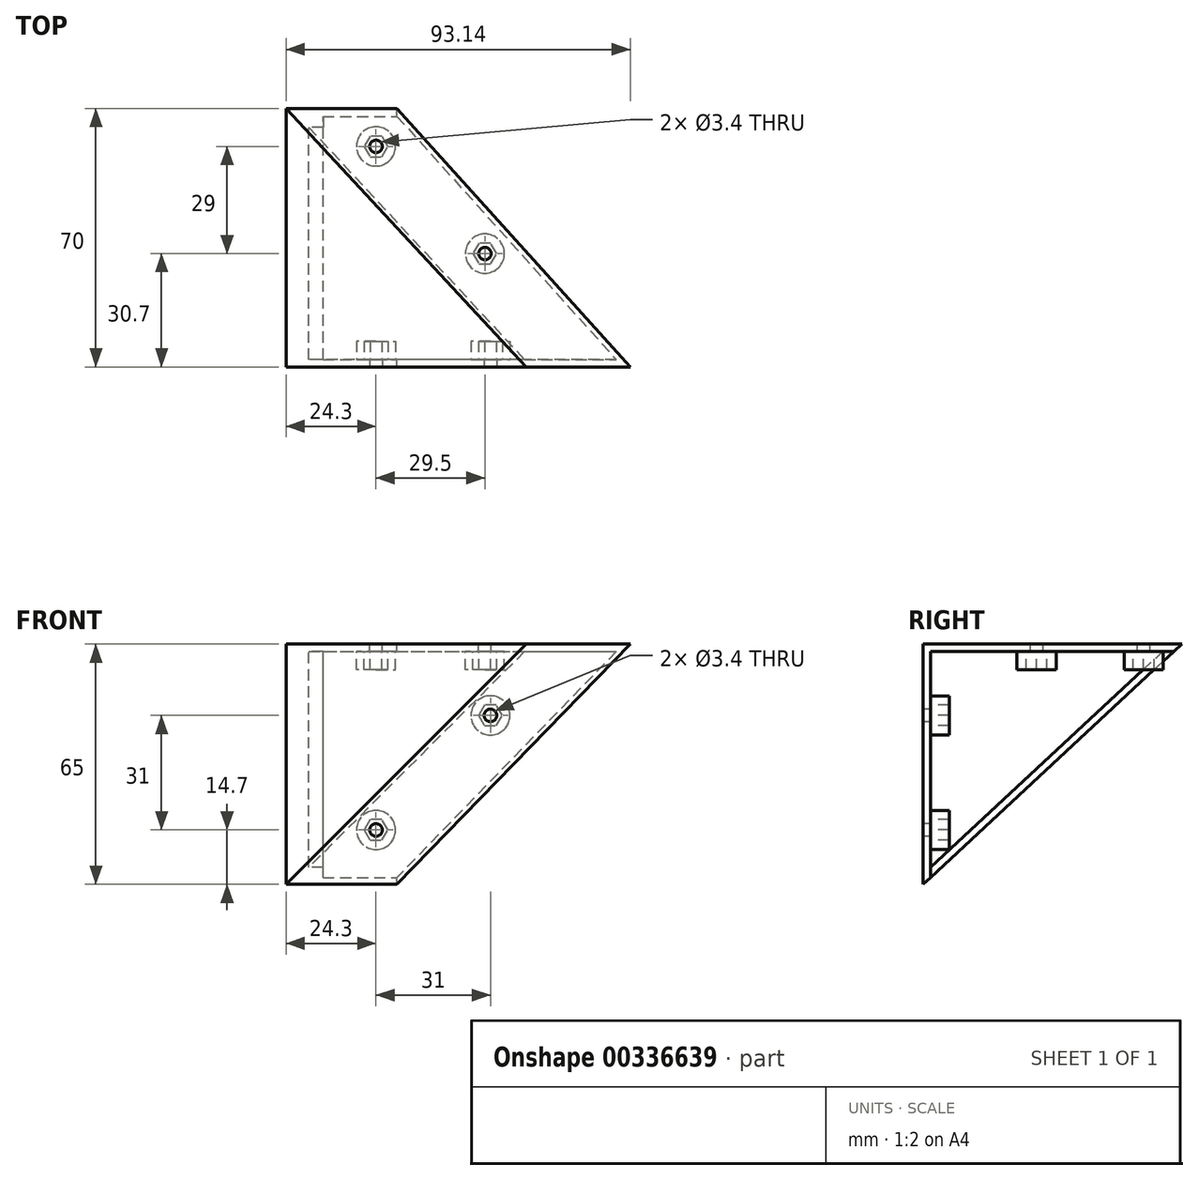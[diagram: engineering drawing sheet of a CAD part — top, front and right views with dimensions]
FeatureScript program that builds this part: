
annotation { "Feature Type Name" : "Feature", "Feature Type Description" : "" }
export const myFeature = defineFeature(function(context is Context, id is Id, definition is map)
    precondition{}
    {
        {
            var Q0;
            Q0=qCreatedBy(makeId("Front.planeOp"),FACE);
            var sketch = newSketch(context, id + "F0", { "sketchPlane" : qUnion([Q0])});
            skLineSegment(sketch, "E0", {"start": v(-300, 0) * mm, "end": v(0, 0) * mm});
            skLineSegment(sketch, "E1", {"start": v(0, 0) * mm, "end": v(0, 175) * mm});
            skLineSegment(sketch, "E2", {"start": v(0, 175) * mm, "end": v(-30, 175) * mm});
            skLineSegment(sketch, "E3", {"start": v(-30, 175) * mm, "end": v(-30, 95) * mm});
            skLineSegment(sketch, "E4", {"start": v(-30, 95) * mm, "end": v(-70, 95) * mm});
            skLineSegment(sketch, "E5", {"start": v(-70, 95) * mm, "end": v(-75, 90) * mm});
            skLineSegment(sketch, "E6", {"start": v(-75, 90) * mm, "end": v(-75, 85) * mm});
            skLineSegment(sketch, "E7", {"start": v(-75, 85) * mm, "end": v(-140, 20) * mm});
            skLineSegment(sketch, "E8", {"start": v(-140, 20) * mm, "end": v(-300, 20) * mm});
            skLineSegment(sketch, "E9", {"start": v(-300, 20) * mm, "end": v(-300, 0) * mm});
            skSolve(sketch);
        }
        {
            var Q0;
            Q0 = qSketchRegion(id + "F0", true);
            extrude(context, id + "F1", {"entities" : qUnion([Q0]), "depth" : 5 * mm, "offsetDistance" : 25 * mm});
        }
        {
            var Q0;
            Q0=makeQuery(id+"F1.opExtrude","SWEPT_FACE",FACE,{"disambiguationData":[OSD([sQuery(id+"F0.wireOp",EDGE,"E0")])]});
            cPlane(context, id + "F2", {"entities" : qUnion([Q0]), "cplaneType" : CPlaneType.OFFSET, "offset" : 85 * mm, "oppositeDirection" : true, "width" : 150 * mm, "height" : 150 * mm});
        }
        {
            var Q0;
            Q0=qCreatedBy(id+"F2.planeOp",FACE);
            var sketch = newSketch(context, id + "F3", { "sketchPlane" : qUnion([Q0])});
            skLineSegment(sketch, "E10", {"start": v(0, 0) * mm, "end": v(-70, 0) * mm});
            skLineSegment(sketch, "E11", {"start": v(-70, 0) * mm, "end": v(-140, -70) * mm});
            skLineSegment(sketch, "E12", {"start": v(-140, -70) * mm, "end": v(-300, -70) * mm});
            skLineSegment(sketch, "E13", {"start": v(-300, -70) * mm, "end": v(-300, -157.82) * mm});
            skLineSegment(sketch, "E14", {"start": v(-300, -157.82) * mm, "end": v(0, -157.82) * mm});
            skLineSegment(sketch, "E15", {"start": v(0, -157.82) * mm, "end": v(0, 0) * mm});
            skSolve(sketch);
        }
        {
            var Q0;
            Q0=makeQuery(id+"F3.imprint","IMPRINT",FACE,{"disambiguationData":[TD([[makeQuery(id+"F3.imprint","IMPRINT",EDGE,{"derivedFrom":sQuery(id+"F3.wireOp",EDGE,"E10")}),1.0]])]});
            extrude(context, id + "F4", {"entities" : qUnion([Q0]), "operationType" : NewBodyOperationType.ADD, "oppositeDirection" : true, "depth" : 5 * mm, "offsetDistance" : 25 * mm});
        }
        {
            var Q0;
            Q0=makeQuery(id+"F4.opExtrude","CAP_VERTEX",VERTEX,{"disambiguationData":[OSD([sQuery(id+"F3.wireOp",EDGE,"E12"),sQuery(id+"F3.wireOp",EDGE,"E13")])],"isStart":true});
            var Q1;
            Q1=sQuery(id+"F0.wireOp",VERTEX,"E9.start");
            var Q2;
            Q2=sQuery(id+"F0.wireOp",VERTEX,"E8.start");
            cPlane(context, id + "F5", {"entities" : qUnion([Q0, Q1, Q2]), "cplaneType" : CPlaneType.THREE_POINT, "offset" : 25 * mm, "width" : 150 * mm, "height" : 150 * mm});
        }
        {
            var Q0;
            Q0=qCreatedBy(id+"F5.planeOp",FACE);
            var sketch = newSketch(context, id + "F6", { "sketchPlane" : qUnion([Q0])});
            skLineSegment(sketch, "E16", {"start": v(-140, -109.13) * mm, "end": v(-140, -13.6) * mm});
            skLineSegment(sketch, "E17", {"start": v(-140, -13.6) * mm, "end": v(-300, -13.6) * mm});
            skLineSegment(sketch, "E18", {"start": v(-300, -13.6) * mm, "end": v(-300, -109.13) * mm});
            skLineSegment(sketch, "E19", {"start": v(-300, -109.13) * mm, "end": v(-140, -109.13) * mm});
            skSolve(sketch);
        }
        {
            var Q0;
            Q0=qSketchRegion(id+"F0",true);
            extrude(context, id + "F7", {"entities" : qUnion([Q0]), "depth" : 5.42 * mm});
        }
        {
            var Q0;
            Q0=qCreatedBy(id+"F5.planeOp",FACE);
            var sketch = newSketch(context, id + "F8", { "sketchPlane" : qUnion([Q0])});
            skLineSegment(sketch, "E20", {"start": v(-140, -109.13) * mm, "end": v(-140, -13.6) * mm});
            skLineSegment(sketch, "E21", {"start": v(-140, -13.6) * mm, "end": v(-110, -13.6) * mm});
            skLineSegment(sketch, "E22", {"start": v(-110, -13.6) * mm, "end": v(-110, -109.13) * mm});
            skLineSegment(sketch, "E23", {"start": v(-110, -109.13) * mm, "end": v(-140, -109.13) * mm});
            skSolve(sketch);
        }
        {
            var Q0;
            Q0=sQuery(id+"F0.wireOp",VERTEX,"E7.start");
            var Q1;
            Q1=sQuery(id+"F8.wireOp",VERTEX,"E20.start");
            var Q2;
            Q2=sQuery(id+"F8.wireOp",VERTEX,"E21.start");
            cPlane(context, id + "F9", {"entities" : qUnion([Q0, Q1, Q2]), "cplaneType" : CPlaneType.THREE_POINT, "offset" : 25 * mm, "width" : 150 * mm, "height" : 150 * mm});
        }
        {
            var Q0;
            Q0=qCreatedBy(id+"F9.planeOp",FACE);
            var sketch = newSketch(context, id + "F10", { "sketchPlane" : qUnion([Q0])});
            skLineSegment(sketch, "E24", {"start": v(145.84, -38.9) * mm, "end": v(62.1, -84.85) * mm});
            skLineSegment(sketch, "E25", {"start": v(62.1, -84.85) * mm, "end": v(62.1, 7.07) * mm});
            skLineSegment(sketch, "E26", {"start": v(62.1, 7.07) * mm, "end": v(145.84, -38.9) * mm});
            skSolve(sketch);
        }
        {
            var Q0;
            Q0 = qSketchRegion(id + "F10", true);
            extrude(context, id + "F11", {"entities" : qUnion([Q0]), "operationType" : NewBodyOperationType.ADD, "depth" : 2 * mm, "offsetDistance" : 25 * mm});
        }
        {
            var Q0;
            Q0=makeQuery(id+"F4.opExtrude","CAP_VERTEX",VERTEX,{"disambiguationData":[OSD([sQuery(id+"F3.wireOp",EDGE,"E10"),sQuery(id+"F3.wireOp",EDGE,"E11")])],"isStart":true});
            var Q1;
            Q1=sQuery(id+"F0.wireOp",VERTEX,"E7.start");
            var Q2;
            Q2=sQuery(id+"F6.wireOp",VERTEX,"E19.end");
            cPlane(context, id + "F12", {"entities" : qUnion([Q0, Q1, Q2]), "cplaneType" : CPlaneType.THREE_POINT, "offset" : 25 * mm, "width" : 150 * mm, "height" : 150 * mm});
        }
        {
            var Q0;
            Q0=qCreatedBy(id+"F12.planeOp",FACE);
            var sketch = newSketch(context, id + "F13", { "sketchPlane" : qUnion([Q0])});
            skLineSegment(sketch, "E27", {"start": v(-70, 0) * mm, "end": v(-75, 0) * mm});
            skLineSegment(sketch, "E28", {"start": v(-75, 0) * mm, "end": v(-140, 70) * mm});
            skLineSegment(sketch, "E29", {"start": v(-140, 70) * mm, "end": v(-70, 0) * mm});
            skSolve(sketch);
        }
        {
            var Q0;
            Q0=makeQuery(id+"F13.imprint","IMPRINT",FACE,{"disambiguationData":[TD([[makeQuery(id+"F13.imprint","IMPRINT",EDGE,{"derivedFrom":sQuery(id+"F13.wireOp",EDGE,"E27")}),-1.0]])]});
            extrude(context, id + "F14", {"entities" : qUnion([Q0]), "oppositeDirection" : true, "depth" : 2 * mm, "offsetDistance" : 25 * mm});
        }
        {
            var Q0;
            Q0=makeQuery(id+"F8.imprint","IMPRINT",FACE,{"disambiguationData":[TD([[makeQuery(id+"F8.imprint","IMPRINT",EDGE,{"derivedFrom":sQuery(id+"F8.wireOp",EDGE,"E20")}),-1.0]])]});
            extrude(context, id + "F15", {"entities" : qUnion([Q0]), "oppositeDirection" : true, "depth" : 2 * mm, "offsetDistance" : 25 * mm});
        }
        {
            var Q0;
            Q0=makeQuery(id+"F0.imprint","IMPRINT",FACE,{"disambiguationData":[TD([[makeQuery(id+"F0.imprint","IMPRINT",EDGE,{"derivedFrom":sQuery(id+"F0.wireOp",EDGE,"E0")}),1.0]])]});
            var sketch = newSketch(context, id + "F16", { "sketchPlane" : qUnion([Q0])});
            skLineSegment(sketch, "E30", {"start": v(-75, 85) * mm, "end": v(-45, 85) * mm});
            skLineSegment(sketch, "E31", {"start": v(-45, 85) * mm, "end": v(-110, 20) * mm});
            skLineSegment(sketch, "E32", {"start": v(-110, 20) * mm, "end": v(-140, 20) * mm});
            skLineSegment(sketch, "E33", {"start": v(-140, 20) * mm, "end": v(-75, 85) * mm});
            skSolve(sketch);
        }
        {
            var Q0;
            Q0=makeQuery(id+"F4.opExtrude","CAP_FACE",FACE,{"disambiguationData":[OSD([sQuery(id+"F3.wireOp",EDGE,"E10"),sQuery(id+"F3.wireOp",EDGE,"E11"),sQuery(id+"F3.wireOp",EDGE,"E12"),sQuery(id+"F3.wireOp",EDGE,"E13"),sQuery(id+"F3.wireOp",EDGE,"E14"),sQuery(id+"F3.wireOp",EDGE,"E15")])],"isStart":true});
            extrude(context, id + "F17", {"entities" : qUnion([Q0]), "operationType" : NewBodyOperationType.REMOVE, "oppositeDirection" : true, "depth" : 102.5 * mm, "offsetDistance" : 25 * mm});
        }
        {
            var Q0;
            Q0=makeQuery(id+"F16.imprint","IMPRINT",FACE,{"disambiguationData":[TD([[makeQuery(id+"F16.imprint","IMPRINT",EDGE,{"derivedFrom":sQuery(id+"F16.wireOp",EDGE,"E30")}),-1.0]])]});
            extrude(context, id + "F18", {"entities" : qUnion([Q0]), "operationType" : NewBodyOperationType.ADD, "oppositeDirection" : true, "depth" : 2 * mm, "offsetDistance" : 25 * mm});
        }
        {
            var Q0;
            Q0=makeQuery(id+"F0.imprint","IMPRINT",FACE,{"disambiguationData":[TD([[makeQuery(id+"F0.imprint","IMPRINT",EDGE,{"derivedFrom":sQuery(id+"F0.wireOp",EDGE,"E0")}),1.0]])]});
            extrude(context, id + "F19", {"entities" : qUnion([Q0]), "operationType" : NewBodyOperationType.REMOVE, "depth" : 239 * mm, "offsetDistance" : 25 * mm});
        }
        {
            var Q0;
            Q0=sQuery(id+"F0.wireOp",VERTEX,"E7.start");
            var Q1;
            Q1=makeQuery(id+"F18.opExtrude","CAP_VERTEX",VERTEX,{"disambiguationData":[OSD([sQuery(id+"F16.wireOp",EDGE,"E30"),sQuery(id+"F16.wireOp",EDGE,"E31")])],"isStart":false});
            var Q2;
            Q2=makeQuery(id+"F15.opExtrude","CAP_VERTEX",VERTEX,{"disambiguationData":[OSD([sQuery(id+"F8.wireOp",EDGE,"E22"),sQuery(id+"F8.wireOp",EDGE,"E23")])],"isStart":true});
            cPlane(context, id + "F20", {"entities" : qUnion([Q0, Q1, Q2]), "cplaneType" : CPlaneType.THREE_POINT, "offset" : 25 * mm, "width" : 150 * mm, "height" : 150 * mm});
        }
        {
            var Q0;
            Q0=qCreatedBy(id+"F20.planeOp",FACE);
            var sketch = newSketch(context, id + "F21", { "sketchPlane" : qUnion([Q0])});
            skLineSegment(sketch, "E34", {"start": v(-45, 0) * mm, "end": v(-110, -70) * mm});
            skLineSegment(sketch, "E35", {"start": v(-110, -70) * mm, "end": v(-140, -70) * mm});
            skLineSegment(sketch, "E36", {"start": v(-140, -70) * mm, "end": v(-75, 0) * mm});
            skLineSegment(sketch, "E37", {"start": v(-75, 0) * mm, "end": v(-45, 0) * mm});
            skSolve(sketch);
        }
        {
            var Q0;
            Q0 = qSketchRegion(id + "F21", true);
            extrude(context, id + "F22", {"entities" : qUnion([Q0]), "operationType" : NewBodyOperationType.ADD, "depth" : 2 * mm, "offsetDistance" : 25 * mm});
        }
        {
            var Q0;
            Q0=sQuery(id+"F6.wireOp",VERTEX,"E17.start");
            var Q1;
            Q1=sQuery(id+"F6.wireOp",VERTEX,"E19.end");
            var Q2;
            {var subQ0=sQuery(id+"F8.wireOp",EDGE,"E22");Q2=makeQuery(id+"F18.boolean.opBoolean","INTERSECT",VERTEX,{"derivedFrom":[makeQuery(id+"F15.opExtrude","CAP_FACE",FACE,{"disambiguationData":[OSD([sQuery(id+"F8.wireOp",EDGE,"E20"),sQuery(id+"F8.wireOp",EDGE,"E21"),subQ0,sQuery(id+"F8.wireOp",EDGE,"E23")])],"isStart":true}),makeQuery(id+"F15.opExtrude","SWEPT_FACE",FACE,{"disambiguationData":[OSD([subQ0])]}),makeQuery(id+"F18.opExtrude","CAP_FACE",FACE,{"disambiguationData":[OSD([sQuery(id+"F16.wireOp",EDGE,"E30"),sQuery(id+"F16.wireOp",EDGE,"E31"),sQuery(id+"F16.wireOp",EDGE,"E32"),sQuery(id+"F16.wireOp",EDGE,"E33")])],"isStart":false})]});}
            cPlane(context, id + "F23", {"entities" : qUnion([Q0, Q1, Q2]), "cplaneType" : CPlaneType.THREE_POINT, "offset" : 25 * mm, "width" : 150 * mm, "height" : 150 * mm});
        }
        {
            var Q0;
            Q0=qCreatedBy(id+"F23.planeOp",FACE);
            var sketch = newSketch(context, id + "F24", { "sketchPlane" : qUnion([Q0])});
            skLineSegment(sketch, "E38", {"start": v(-152.04, 9.78) * mm, "end": v(-152.04, 115.97) * mm});
            skLineSegment(sketch, "E39", {"start": v(-152.04, 115.97) * mm, "end": v(-52.48, 115.97) * mm});
            skLineSegment(sketch, "E40", {"start": v(-52.48, 115.97) * mm, "end": v(-52.48, 8.15) * mm});
            skLineSegment(sketch, "E41", {"start": v(-52.48, 8.15) * mm, "end": v(-152.04, 9.78) * mm});
            skSolve(sketch);
        }
        {
            var Q0;
            Q0 = qSketchRegion(id + "F24", true);
            extrude(context, id + "F25", {"entities" : qUnion([Q0]), "operationType" : NewBodyOperationType.REMOVE, "oppositeDirection" : true, "depth" : 25 * mm, "offsetDistance" : 25 * mm});
        }
        {
            var Q0;
            Q0=sQuery(id+"F6.wireOp",VERTEX,"E19.end");
            var Q1;
            Q1=sQuery(id+"F6.wireOp",VERTEX,"E17.start");
            var Q2;
            Q2=sQuery(id+"F0.wireOp",VERTEX,"E7.start");
            cPlane(context, id + "F26", {"entities" : qUnion([Q0, Q1, Q2]), "cplaneType" : CPlaneType.THREE_POINT, "offset" : 25 * mm, "width" : 150 * mm, "height" : 150 * mm});
        }
        {
            var Q0;
            Q0=qCreatedBy(id+"F26.planeOp",FACE);
            var sketch = newSketch(context, id + "F27", { "sketchPlane" : qUnion([Q0])});
            skLineSegment(sketch, "E42.bottom", {"start": v(59.1, -93.53) * mm, "end": v(160.86, -93.53) * mm});
            skLineSegment(sketch, "E42.top", {"start": v(59.1, -19.2) * mm, "end": v(160.86, -19.2) * mm});
            skLineSegment(sketch, "E42.left", {"start": v(59.1, -93.53) * mm, "end": v(59.1, -19.2) * mm});
            skLineSegment(sketch, "E42.right", {"start": v(160.86, -93.53) * mm, "end": v(160.86, -19.2) * mm});
            skPoint(sketch, "E42.middle", {"position": v(109.98, -56.36) * mm});
            skSolve(sketch);
        }
        {
            var Q0;
            Q0 = qSketchRegion(id + "F27", true);
            extrude(context, id + "F28", {"entities" : qUnion([Q0]), "operationType" : NewBodyOperationType.REMOVE, "oppositeDirection" : true, "depth" : 25 * mm, "offsetDistance" : 25 * mm});
        }
        {
            var Q0;
            {var subQ0=sQuery(id+"F13.wireOp",EDGE,"E29");var subQ3=sQuery(id+"F16.wireOp",EDGE,"E30");var subQ8=sQuery(id+"F16.wireOp",EDGE,"E31");var subQ9=makeQuery(id+"F18.opExtrude","SWEPT_FACE",FACE,{"disambiguationData":[OSD([subQ8])]});var subQ10=sQuery(id+"F16.wireOp",EDGE,"E32");Q0=makeQuery(id+"F22.boolean.opBoolean","INTERSECT",VERTEX,{"derivedFrom":[subQ9,makeQuery(id+"F18.boolean.opBoolean","SPLIT",FACE,{"disambiguationData":[TD([makeQuery(id+"F14.opExtrude","SWEPT_FACE",FACE,{"disambiguationData":[OSD([subQ0])]})])],"derivedFrom":makeQuery(id+"F18.opExtrude","CAP_FACE",FACE,{"disambiguationData":[OSD([subQ3,subQ8,subQ10,sQuery(id+"F16.wireOp",EDGE,"E33")])],"isStart":false})}),makeQuery(id+"F22.opExtrude","CAP_FACE",FACE,{"disambiguationData":[OSD([sQuery(id+"F21.wireOp",EDGE,"E34"),sQuery(id+"F21.wireOp",EDGE,"E35"),sQuery(id+"F21.wireOp",EDGE,"E36"),sQuery(id+"F21.wireOp",EDGE,"E37")])],"isStart":false})]});}
            var Q1;
            Q1=makeQuery(id+"F22.boolean.opBoolean","INTERSECT",VERTEX,{"derivedFrom":[makeQuery(id+"F18.opExtrude","SWEPT_FACE",FACE,{"disambiguationData":[OSD([sQuery(id+"F16.wireOp",EDGE,"E31")])]}),makeQuery(id+"F22.opExtrude","CAP_FACE",FACE,{"disambiguationData":[OSD([sQuery(id+"F21.wireOp",EDGE,"E34"),sQuery(id+"F21.wireOp",EDGE,"E35"),sQuery(id+"F21.wireOp",EDGE,"E36"),sQuery(id+"F21.wireOp",EDGE,"E37")])],"isStart":false})]});
            var Q2;
            {var subQ0=sQuery(id+"F13.wireOp",EDGE,"E29");var subQ3=sQuery(id+"F16.wireOp",EDGE,"E30");var subQ8=sQuery(id+"F16.wireOp",EDGE,"E31");var subQ9=sQuery(id+"F16.wireOp",EDGE,"E32");Q2=makeQuery(id+"F22.boolean.opBoolean","INTERSECT",VERTEX,{"derivedFrom":[makeQuery(id+"F18.boolean.opBoolean","SPLIT",FACE,{"disambiguationData":[TD([makeQuery(id+"F14.opExtrude","SWEPT_FACE",FACE,{"disambiguationData":[OSD([subQ0])]})])],"derivedFrom":makeQuery(id+"F18.opExtrude","CAP_FACE",FACE,{"disambiguationData":[OSD([subQ3,subQ8,subQ9,sQuery(id+"F16.wireOp",EDGE,"E33")])],"isStart":false})}),makeQuery(id+"F22.opExtrude","SWEPT_FACE",FACE,{"disambiguationData":[OSD([sQuery(id+"F21.wireOp",EDGE,"E34")])]})]});}
            cPlane(context, id + "F29", {"entities" : qUnion([Q0, Q1, Q2]), "cplaneType" : CPlaneType.THREE_POINT, "offset" : 25 * mm, "width" : 150 * mm, "height" : 150 * mm});
        }
        {
            var Q0;
            Q0=qCreatedBy(id+"F29.planeOp",FACE);
            var sketch = newSketch(context, id + "F30", { "sketchPlane" : qUnion([Q0])});
            skLineSegment(sketch, "E43.bottom", {"start": v(-0.77, 81.9) * mm, "end": v(2.8, 81.9) * mm});
            skLineSegment(sketch, "E43.top", {"start": v(-0.77, 79.04) * mm, "end": v(2.8, 79.04) * mm});
            skLineSegment(sketch, "E43.left", {"start": v(-0.77, 81.9) * mm, "end": v(-0.77, 79.04) * mm});
            skLineSegment(sketch, "E43.right", {"start": v(2.8, 81.9) * mm, "end": v(2.8, 79.04) * mm});
            skPoint(sketch, "E43.middle", {"position": v(1, 80.46) * mm});
            skSolve(sketch);
        }
        {
            var Q0;
            Q0 = qSketchRegion(id + "F30", true);
            extrude(context, id + "F31", {"entities" : qUnion([Q0]), "operationType" : NewBodyOperationType.REMOVE, "depth" : 25 * mm, "offsetDistance" : 25 * mm});
        }
        {
            var Q0;
            Q0=makeQuery(id+"F18.boolean.opBoolean","MERGE",VERTEX,{"derivedFrom":[makeQuery(id+"F15.opExtrude","CAP_VERTEX",VERTEX,{"disambiguationData":[OSD([sQuery(id+"F8.wireOp",EDGE,"E21"),sQuery(id+"F8.wireOp",EDGE,"E22")])],"isStart":true}),makeQuery(id+"F18.opExtrude","CAP_VERTEX",VERTEX,{"disambiguationData":[OSD([sQuery(id+"F16.wireOp",EDGE,"E31"),sQuery(id+"F16.wireOp",EDGE,"E32")])],"isStart":true})]});
            var Q1;
            Q1=makeQuery(id+"F22.boolean.opBoolean","MERGE",VERTEX,{"derivedFrom":[makeQuery(id+"F15.opExtrude","CAP_VERTEX",VERTEX,{"disambiguationData":[OSD([sQuery(id+"F8.wireOp",EDGE,"E22"),sQuery(id+"F8.wireOp",EDGE,"E23")])],"isStart":true}),makeQuery(id+"F22.opExtrude","CAP_VERTEX",VERTEX,{"disambiguationData":[OSD([sQuery(id+"F21.wireOp",EDGE,"E34"),sQuery(id+"F21.wireOp",EDGE,"E35")])],"isStart":true})]});
            var Q2;
            {var subQ0=sQuery(id+"F21.wireOp",EDGE,"E37");Q2=makeQuery(id+"F31.boolean.opBoolean","INTERSECT",VERTEX,{"derivedFrom":[makeQuery(id+"F22.boolean.opBoolean","MERGE",FACE,{"derivedFrom":[makeQuery(id+"F17.boolean.opBoolean","COPY",FACE,{"derivedFrom":makeQuery(id+"F17.opExtrude","CAP_FACE",FACE,{"disambiguationData":[OSD([sQuery(id+"F3.wireOp",EDGE,"E10"),sQuery(id+"F3.wireOp",EDGE,"E11"),sQuery(id+"F3.wireOp",EDGE,"E12"),sQuery(id+"F3.wireOp",EDGE,"E13"),sQuery(id+"F3.wireOp",EDGE,"E14"),sQuery(id+"F3.wireOp",EDGE,"E15")])],"isStart":true})}),makeQuery(id+"F18.boolean.opBoolean","MERGE",FACE,{"derivedFrom":[makeQuery(id+"F14.opExtrude","CAP_FACE",FACE,{"disambiguationData":[OSD([sQuery(id+"F13.wireOp",EDGE,"E27"),sQuery(id+"F13.wireOp",EDGE,"E28"),sQuery(id+"F13.wireOp",EDGE,"E29")])],"isStart":true}),makeQuery(id+"F18.opExtrude","SWEPT_FACE",FACE,{"disambiguationData":[OSD([sQuery(id+"F16.wireOp",EDGE,"E30")])]})]}),makeQuery(id+"F22.opExtrude","CAP_FACE",FACE,{"disambiguationData":[OSD([sQuery(id+"F21.wireOp",EDGE,"E34"),sQuery(id+"F21.wireOp",EDGE,"E35"),sQuery(id+"F21.wireOp",EDGE,"E36"),subQ0])],"isStart":true})]}),makeQuery(id+"F22.boolean.opBoolean","MERGE",FACE,{"derivedFrom":[makeQuery(id+"F19.boolean.opBoolean","COPY",FACE,{"derivedFrom":makeQuery(id+"F19.opExtrude","CAP_FACE",FACE,{"disambiguationData":[OSD([sQuery(id+"F0.wireOp",EDGE,"E0"),sQuery(id+"F0.wireOp",EDGE,"E1"),sQuery(id+"F0.wireOp",EDGE,"E2"),sQuery(id+"F0.wireOp",EDGE,"E3"),sQuery(id+"F0.wireOp",EDGE,"E4"),sQuery(id+"F0.wireOp",EDGE,"E5"),sQuery(id+"F0.wireOp",EDGE,"E6"),sQuery(id+"F0.wireOp",EDGE,"E7"),sQuery(id+"F0.wireOp",EDGE,"E8"),sQuery(id+"F0.wireOp",EDGE,"E9")])],"isStart":true})}),makeQuery(id+"F22.opExtrude","SWEPT_FACE",FACE,{"disambiguationData":[OSD([subQ0])]})]}),makeQuery(id+"F31.opExtrude","CAP_FACE",FACE,{"disambiguationData":[OSD([sQuery(id+"F30.wireOp",EDGE,"E43.bottom"),sQuery(id+"F30.wireOp",EDGE,"E43.top"),sQuery(id+"F30.wireOp",EDGE,"E43.left"),sQuery(id+"F30.wireOp",EDGE,"E43.right")])],"isStart":true})]});}
            cPlane(context, id + "F32", {"entities" : qUnion([Q0, Q1, Q2]), "cplaneType" : CPlaneType.THREE_POINT, "offset" : 25 * mm, "width" : 150 * mm, "height" : 150 * mm});
        }
        {
            var Q0;
            Q0=qCreatedBy(id+"F32.planeOp",FACE);
            var sketch = newSketch(context, id + "F33", { "sketchPlane" : qUnion([Q0])});
            skLineSegment(sketch, "E44.bottom", {"start": v(-154.45, -75.64) * mm, "end": v(13.54, -75.64) * mm});
            skLineSegment(sketch, "E44.top", {"start": v(-154.45, 59.94) * mm, "end": v(13.54, 59.94) * mm});
            skLineSegment(sketch, "E44.left", {"start": v(-154.45, -75.64) * mm, "end": v(-154.45, 59.94) * mm});
            skLineSegment(sketch, "E44.right", {"start": v(13.54, -75.64) * mm, "end": v(13.54, 59.94) * mm});
            skPoint(sketch, "E44.middle", {"position": v(-70.46, -7.85) * mm});
            skSolve(sketch);
        }
        {
            var Q0;
            Q0 = qSketchRegion(id + "F33", true);
            extrude(context, id + "F34", {"entities" : qUnion([Q0]), "operationType" : NewBodyOperationType.REMOVE, "oppositeDirection" : true, "depth" : 25 * mm, "offsetDistance" : 25 * mm});
        }
        {
            var Q0;
            Q0=makeQuery(id+"F17.boolean.opBoolean","COPY",FACE,{"derivedFrom":makeQuery(id+"F17.opExtrude","SWEPT_FACE",FACE,{"disambiguationData":[OSD([sQuery(id+"F3.wireOp",EDGE,"E11")])]})});
            extrude(context, id + "F35", {"entities" : qUnion([Q0]), "operationType" : NewBodyOperationType.REMOVE, "oppositeDirection" : true, "depth" : 25 * mm, "offsetDistance" : 25 * mm});
        }
        {
            var Q0;
            Q0=makeQuery(id+"F3.imprint","IMPRINT",FACE,{"disambiguationData":[TD([[makeQuery(id+"F3.imprint","IMPRINT",EDGE,{"derivedFrom":sQuery(id+"F3.wireOp",EDGE,"E10")}),1.0]])]});
            extrude(context, id + "F36", {"entities" : qUnion([Q0]), "operationType" : NewBodyOperationType.ADD, "oppositeDirection" : true, "depth" : 5 * mm, "offsetDistance" : 25 * mm});
        }
        {
            var Q0;
            Q0=makeQuery(id+"F0.imprint","IMPRINT",FACE,{"disambiguationData":[TD([[makeQuery(id+"F0.imprint","IMPRINT",EDGE,{"derivedFrom":sQuery(id+"F0.wireOp",EDGE,"E0")}),1.0]])]});
            extrude(context, id + "F37", {"entities" : qUnion([Q0]), "operationType" : NewBodyOperationType.ADD, "depth" : 5 * mm, "offsetDistance" : 25 * mm});
        }
        {
            var Q0;
            Q0=makeQuery(id+"F6.imprint","IMPRINT",FACE,{"disambiguationData":[TD([[makeQuery(id+"F6.imprint","IMPRINT",EDGE,{"derivedFrom":sQuery(id+"F6.wireOp",EDGE,"E16")}),1.0]])]});
            extrude(context, id + "F38", {"entities" : qUnion([Q0]), "depth" : 5 * mm, "offsetDistance" : 25 * mm});
        }
        {
            var Q0;
            Q0=makeQuery(id+"F37.opExtrude","CAP_FACE",FACE,{"disambiguationData":[OSD([sQuery(id+"F0.wireOp",EDGE,"E0"),sQuery(id+"F0.wireOp",EDGE,"E1"),sQuery(id+"F0.wireOp",EDGE,"E2"),sQuery(id+"F0.wireOp",EDGE,"E3"),sQuery(id+"F0.wireOp",EDGE,"E4"),sQuery(id+"F0.wireOp",EDGE,"E5"),sQuery(id+"F0.wireOp",EDGE,"E6"),sQuery(id+"F0.wireOp",EDGE,"E7"),sQuery(id+"F0.wireOp",EDGE,"E8"),sQuery(id+"F0.wireOp",EDGE,"E9")])],"isStart":false});
            var sketch = newSketch(context, id + "F39", { "sketchPlane" : qUnion([Q0])});
            skCircle(sketch, "E45", {"center": v(-115.7, 34.7) * mm, "radius": 1.7 * mm});
            skCircle(sketch, "E46", {"center": v(-84.7, 65.7) * mm, "radius": 1.7 * mm});
            skSolve(sketch);
        }
        {
            var Q0;
            Q0=makeQuery(id+"F39.imprint","IMPRINT",FACE,{"disambiguationData":[TD([[makeQuery(id+"F39.imprint","IMPRINT",EDGE,{"derivedFrom":sQuery(id+"F39.wireOp",EDGE,"E45")}),1.0]])]});
            var Q1;
            Q1=makeQuery(id+"F39.imprint","IMPRINT",FACE,{"disambiguationData":[TD([[makeQuery(id+"F39.imprint","IMPRINT",EDGE,{"derivedFrom":sQuery(id+"F39.wireOp",EDGE,"E46")}),1.0]])]});
            extrude(context, id + "F40", {"entities" : qUnion([Q0, Q1]), "operationType" : NewBodyOperationType.REMOVE, "oppositeDirection" : true, "depth" : 9.9 * mm, "offsetDistance" : 25 * mm});
        }
        {
            var Q0;
            Q0=makeQuery(id+"F15.opExtrude","SWEPT_FACE",FACE,{"disambiguationData":[OSD([sQuery(id+"F8.wireOp",EDGE,"E22")])]});
            extrude(context, id + "F41", {"entities" : qUnion([Q0]), "operationType" : NewBodyOperationType.REMOVE, "oppositeDirection" : true, "depth" : 20 * mm, "offsetDistance" : 25 * mm});
        }
        {
            var Q0;
            Q0=makeQuery(id+"F36.opExtrude","CAP_FACE",FACE,{"disambiguationData":[OSD([sQuery(id+"F3.wireOp",EDGE,"E10"),sQuery(id+"F3.wireOp",EDGE,"E11"),sQuery(id+"F3.wireOp",EDGE,"E12"),sQuery(id+"F3.wireOp",EDGE,"E13"),sQuery(id+"F3.wireOp",EDGE,"E14"),sQuery(id+"F3.wireOp",EDGE,"E15")])],"isStart":false});
            var sketch = newSketch(context, id + "F42", { "sketchPlane" : qUnion([Q0])});
            skCircle(sketch, "E47", {"center": v(-86.2, 30.7) * mm, "radius": 1.7 * mm});
            skCircle(sketch, "E48", {"center": v(-115.7, 59.7) * mm, "radius": 1.7 * mm});
            skSolve(sketch);
        }
        {
            var Q0;
            Q0 = qSketchRegion(id + "F42", true);
            extrude(context, id + "F43", {"entities" : qUnion([Q0]), "operationType" : NewBodyOperationType.REMOVE, "oppositeDirection" : true, "depth" : 25 * mm, "offsetDistance" : 25 * mm});
        }
        {
            var Q0;
            {var subQ0=sQuery(id+"F16.wireOp",EDGE,"E33");var subQ1=sQuery(id+"F16.wireOp",EDGE,"E32");var subQ2=sQuery(id+"F16.wireOp",EDGE,"E31");var subQ3=sQuery(id+"F16.wireOp",EDGE,"E30");var subQ4=sQuery(id+"F8.wireOp",EDGE,"E22");var subQ12=sQuery(id+"F13.wireOp",EDGE,"E29");var subQ17=makeQuery(id+"F15.opExtrude","SWEPT_FACE",FACE,{"disambiguationData":[OSD([subQ4])]});Q0=makeQuery(id+"F41.boolean.opBoolean","MERGE",FACE,{"derivedFrom":[makeQuery(id+"F22.boolean.opBoolean","SPLIT",FACE,{"disambiguationData":[TD([subQ17])],"derivedFrom":makeQuery(id+"F18.boolean.opBoolean","SPLIT",FACE,{"disambiguationData":[TD([makeQuery(id+"F14.opExtrude","SWEPT_FACE",FACE,{"disambiguationData":[OSD([subQ12])]})])],"derivedFrom":makeQuery(id+"F18.opExtrude","CAP_FACE",FACE,{"disambiguationData":[OSD([subQ3,subQ2,subQ1,subQ0])],"isStart":false})})}),makeQuery(id+"F41.opExtrude","SWEPT_FACE",FACE,{"disambiguationData":[OSD([subQ4,subQ3,subQ2,subQ1,subQ0])]})]});}
            var sketch = newSketch(context, id + "F44", { "sketchPlane" : qUnion([Q0])});
            skCircle(sketch, "E49.cCircle", {"center": v(84.7, 65.7) * mm, "radius": 2.8 * mm, "construction": true});
            skLineSegment(sketch, "E49.0", {"start": v(86.32, 62.9) * mm, "end": v(83.08, 62.9) * mm});
            skLineSegment(sketch, "E49.1", {"start": v(83.08, 62.9) * mm, "end": v(81.47, 65.7) * mm});
            skLineSegment(sketch, "E49.2", {"start": v(81.47, 65.7) * mm, "end": v(83.08, 68.5) * mm});
            skLineSegment(sketch, "E49.3", {"start": v(83.08, 68.5) * mm, "end": v(86.32, 68.5) * mm});
            skLineSegment(sketch, "E49.4", {"start": v(86.32, 68.5) * mm, "end": v(87.93, 65.7) * mm});
            skLineSegment(sketch, "E49.5", {"start": v(87.93, 65.7) * mm, "end": v(86.32, 62.9) * mm});
            skPoint(sketch, "E49.0.midPoint", {"position": v(84.7, 62.9) * mm});
            skCircle(sketch, "E50.cCircle", {"center": v(115.7, 34.7) * mm, "radius": 2.8 * mm, "construction": true});
            skLineSegment(sketch, "E50.0", {"start": v(117.32, 31.9) * mm, "end": v(114.08, 31.9) * mm});
            skLineSegment(sketch, "E50.1", {"start": v(114.08, 31.9) * mm, "end": v(112.47, 34.7) * mm});
            skLineSegment(sketch, "E50.2", {"start": v(112.47, 34.7) * mm, "end": v(114.08, 37.5) * mm});
            skLineSegment(sketch, "E50.3", {"start": v(114.08, 37.5) * mm, "end": v(117.32, 37.5) * mm});
            skLineSegment(sketch, "E50.4", {"start": v(117.32, 37.5) * mm, "end": v(118.93, 34.7) * mm});
            skLineSegment(sketch, "E50.5", {"start": v(118.93, 34.7) * mm, "end": v(117.32, 31.9) * mm});
            skPoint(sketch, "E50.0.midPoint", {"position": v(115.7, 31.9) * mm});
            skCircle(sketch, "E51", {"center": v(115.7, 34.7) * mm, "radius": 5.3 * mm});
            skCircle(sketch, "E52", {"center": v(84.7, 65.7) * mm, "radius": 5.3 * mm});
            skSolve(sketch);
        }
        {
            var Q0;
            Q0 = qSketchRegion(id + "F44", true);
            extrude(context, id + "F45", {"entities" : qUnion([Q0]), "operationType" : NewBodyOperationType.ADD, "depth" : 5 * mm, "offsetDistance" : 25 * mm});
        }
        {
            var Q0;
            {var subQ0=sQuery(id+"F21.wireOp",EDGE,"E37");var subQ1=sQuery(id+"F21.wireOp",EDGE,"E36");var subQ2=sQuery(id+"F21.wireOp",EDGE,"E35");var subQ3=sQuery(id+"F21.wireOp",EDGE,"E34");var subQ4=sQuery(id+"F13.wireOp",EDGE,"E29");Q0=makeQuery(id+"F41.boolean.opBoolean","MERGE",FACE,{"derivedFrom":[makeQuery(id+"F22.boolean.opBoolean","MERGE",FACE,{"derivedFrom":[makeQuery(id+"F18.boolean.opBoolean","SPLIT",FACE,{"disambiguationData":[TD([makeQuery(id+"F11.opExtrude","CAP_FACE",FACE,{"disambiguationData":[OSD([sQuery(id+"F10.wireOp",EDGE,"E24"),sQuery(id+"F10.wireOp",EDGE,"E25"),sQuery(id+"F10.wireOp",EDGE,"E26")])],"isStart":false})])],"derivedFrom":makeQuery(id+"F14.opExtrude","CAP_FACE",FACE,{"disambiguationData":[OSD([sQuery(id+"F13.wireOp",EDGE,"E27"),sQuery(id+"F13.wireOp",EDGE,"E28"),subQ4])],"isStart":false})}),makeQuery(id+"F22.opExtrude","CAP_FACE",FACE,{"disambiguationData":[OSD([subQ3,subQ2,subQ1,subQ0])],"isStart":false})]}),makeQuery(id+"F41.opExtrude","SWEPT_FACE",FACE,{"disambiguationData":[OSD([sQuery(id+"F8.wireOp",EDGE,"E22"),subQ3,subQ2,subQ1,subQ0])]})]});}
            var sketch = newSketch(context, id + "F46", { "sketchPlane" : qUnion([Q0])});
            skCircle(sketch, "E53.cCircle", {"center": v(-115.7, -59.7) * mm, "radius": 2.8 * mm, "construction": true});
            skLineSegment(sketch, "E53.0", {"start": v(-114.08, -62.5) * mm, "end": v(-117.32, -62.5) * mm});
            skLineSegment(sketch, "E53.1", {"start": v(-117.32, -62.5) * mm, "end": v(-118.93, -59.7) * mm});
            skLineSegment(sketch, "E53.2", {"start": v(-118.93, -59.7) * mm, "end": v(-117.32, -56.9) * mm});
            skLineSegment(sketch, "E53.3", {"start": v(-117.32, -56.9) * mm, "end": v(-114.08, -56.9) * mm});
            skLineSegment(sketch, "E53.4", {"start": v(-114.08, -56.9) * mm, "end": v(-112.47, -59.7) * mm});
            skLineSegment(sketch, "E53.5", {"start": v(-112.47, -59.7) * mm, "end": v(-114.08, -62.5) * mm});
            skPoint(sketch, "E53.0.midPoint", {"position": v(-115.7, -62.5) * mm});
            skCircle(sketch, "E54.cCircle", {"center": v(-86.2, -30.7) * mm, "radius": 2.8 * mm, "construction": true});
            skLineSegment(sketch, "E54.0", {"start": v(-84.58, -33.5) * mm, "end": v(-87.82, -33.5) * mm});
            skLineSegment(sketch, "E54.1", {"start": v(-87.82, -33.5) * mm, "end": v(-89.43, -30.7) * mm});
            skLineSegment(sketch, "E54.2", {"start": v(-89.43, -30.7) * mm, "end": v(-87.82, -27.9) * mm});
            skLineSegment(sketch, "E54.3", {"start": v(-87.82, -27.9) * mm, "end": v(-84.58, -27.9) * mm});
            skLineSegment(sketch, "E54.4", {"start": v(-84.58, -27.9) * mm, "end": v(-82.97, -30.7) * mm});
            skLineSegment(sketch, "E54.5", {"start": v(-82.97, -30.7) * mm, "end": v(-84.58, -33.5) * mm});
            skPoint(sketch, "E54.0.midPoint", {"position": v(-86.2, -33.5) * mm});
            skCircle(sketch, "E55", {"center": v(-115.7, -59.7) * mm, "radius": 5.3 * mm});
            skCircle(sketch, "E56", {"center": v(-86.2, -30.7) * mm, "radius": 5.3 * mm});
            skSolve(sketch);
        }
        {
            var Q0;
            Q0 = qSketchRegion(id + "F46", true);
            extrude(context, id + "F47", {"entities" : qUnion([Q0]), "operationType" : NewBodyOperationType.ADD, "depth" : 5 * mm, "offsetDistance" : 25 * mm});
        }
        {
            var Q0;
            Q0=makeQuery(id+"F6.imprint","IMPRINT",FACE,{"disambiguationData":[TD([[makeQuery(id+"F6.imprint","IMPRINT",EDGE,{"derivedFrom":sQuery(id+"F6.wireOp",EDGE,"E16")}),1.0]])]});
            extrude(context, id + "F48", {"entities" : qUnion([Q0]), "operationType" : NewBodyOperationType.REMOVE, "depth" : 154 * mm, "offsetDistance" : 25 * mm});
        }
        {
            var Q0;
            Q0=makeQuery(id+"F39.imprint","IMPRINT",FACE,{"disambiguationData":[TD([[makeQuery(id+"F39.imprint","IMPRINT",EDGE,{"derivedFrom":sQuery(id+"F39.wireOp",EDGE,"E45")}),-1.0]])]});
            extrude(context, id + "F49", {"entities" : qUnion([Q0]), "operationType" : NewBodyOperationType.REMOVE, "oppositeDirection" : true, "depth" : 5 * mm, "offsetDistance" : 25 * mm});
        }
        {
            var Q0;
            Q0=makeQuery(id+"F42.imprint","IMPRINT",FACE,{"disambiguationData":[TD([[makeQuery(id+"F42.imprint","IMPRINT",EDGE,{"derivedFrom":sQuery(id+"F42.wireOp",EDGE,"E47")}),-1.0]])]});
            extrude(context, id + "F50", {"entities" : qUnion([Q0]), "operationType" : NewBodyOperationType.REMOVE, "oppositeDirection" : true, "depth" : 5 * mm, "offsetDistance" : 25 * mm});
        }
    });
